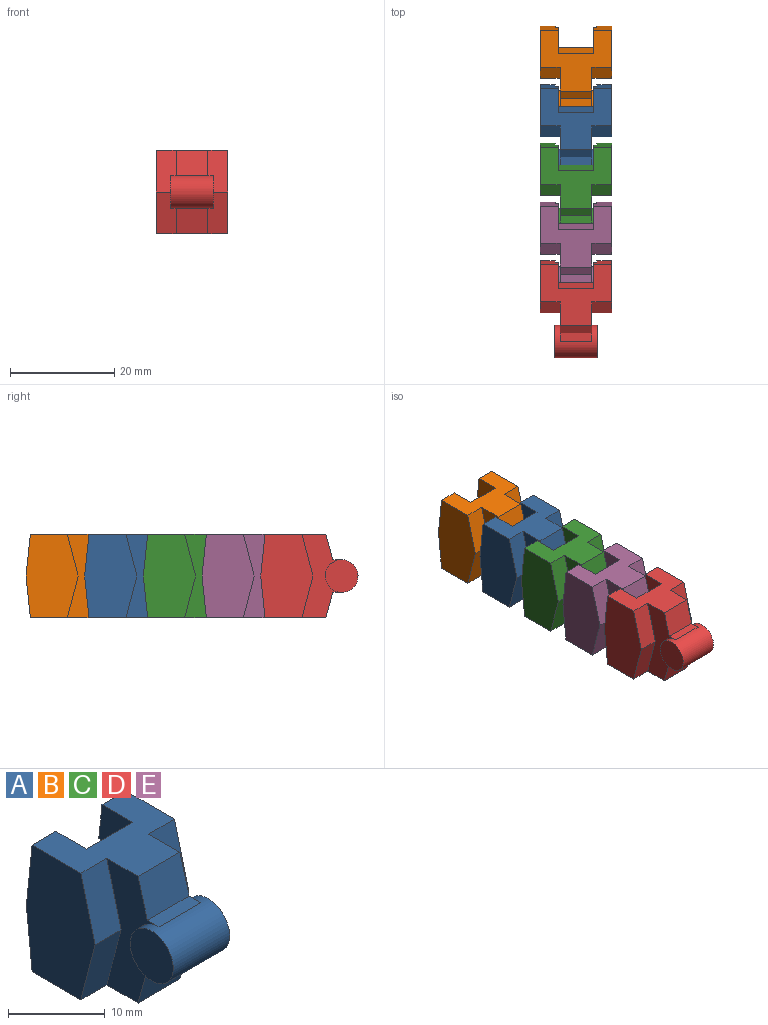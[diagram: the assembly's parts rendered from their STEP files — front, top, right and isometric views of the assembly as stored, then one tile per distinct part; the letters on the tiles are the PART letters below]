
ASSEMBLY  parts=5 mates=4
PART A: 36 faces, bbox 13.7x18.7x16 mm
  f0: plane 8x3.47mm, normal (0,0.99,-0.1), area 25.7mm2, adj f8,f12,f17,f21,f23,f24
  f1: plane 8x3.47mm, normal (0,0.99,-0.1), area 25.7mm2, adj f9,f11,f18,f21,f23,f25
  f2: cylinder r=3.14mm len=8.23mm, axis (-1,0,0), area 102.1mm2, adj f3,f4,f5,f6,f19,f31
  f3: plane 6.27x6.27mm, normal (1,0,0), area 30.9mm2, adj f2
  f4: plane 6.27x6.27mm, normal (-1,0,0), area 30.9mm2, adj f2
  f5: plane 16x7.62mm, normal (1,0,0), area 66.7mm2, adj f2,f10,f19,f20,f21,f27,f31,f32
  f6: plane 16x7.62mm, normal (-1,0,0), area 66.7mm2, adj f2,f7,f19,f20,f21,f26,f31,f32
  f7: plane 8x3.78mm, normal (0,-0.97,-0.25), area 31.3mm2, adj f6,f8,f21,f26
  f8: plane 16x10.03mm, normal (-1,0,0), area 137.2mm2, adj f0,f7,f21,f24,f26,f33
  f9: plane 16x10.03mm, normal (1,0,0), area 137.2mm2, adj f1,f10,f21,f25,f27,f33
  f10: plane 8x3.78mm, normal (0,-0.97,-0.25), area 31.3mm2, adj f5,f9,f21,f27
  f11: plane 7.04x4.29mm, normal (-1,0,0), area 9.5mm2, adj f1,f15,f23,f25,f35
  f12: plane 7.04x4.29mm, normal (1,0,0), area 9.5mm2, adj f0,f15,f23,f24,f35
  f13: plane 7.04x7.04mm, normal (1,0,0), area 38.9mm2, adj f15
  f14: plane 7.04x7.04mm, normal (-1,0,0), area 38.9mm2, adj f15
  f15: cylinder r=3.52mm len=9.3mm, axis (-1,0,0), area 117.3mm2, adj f11,f12,f13,f14,f23,f35
  f16: plane 6.73x0.11mm, normal (0,1,0), area 0.8mm2, adj f17,f18,f22,f23
  f17: plane 4.94x4.48mm, normal (1,0,0), area 18.6mm2, adj f0,f16,f21,f22,f23
  f18: plane 4.94x4.48mm, normal (-1,0,0), area 18.6mm2, adj f1,f16,f21,f22,f23
  f19: plane 6.1x1.7mm, normal (0,0,-1), area 10.4mm2, adj f2,f5,f6,f20
  f20: plane 6.1x4.86mm, normal (0,-0.96,-0.27), area 30.8mm2, adj f5,f6,f19,f21
  f21: plane 13.67x11.68mm, normal (0,0,-1), area 95mm2, adj f0,f1,f5,f6,f7,f8,f9,f10
  f22: plane 6.73x4.37mm, normal (0,0.97,-0.24), area 30.3mm2, adj f16,f17,f18,f21
  f23: plane 7.98x3.92mm, normal (0,0,1), area 5.3mm2, adj f0,f1,f11,f12,f15,f16,f17,f18
  f24: plane 8x3.47mm, normal (0,0.99,0.1), area 25.7mm2, adj f0,f8,f12,f29,f33,f35
  f25: plane 8x3.47mm, normal (0,0.99,0.1), area 25.7mm2, adj f1,f9,f11,f30,f33,f35
  f26: plane 8x3.78mm, normal (0,-0.97,0.25), area 31.3mm2, adj f6,f7,f8,f33
  f27: plane 8x3.78mm, normal (0,-0.97,0.25), area 31.3mm2, adj f5,f9,f10,f33
  f28: plane 6.73x0.11mm, normal (0,1,0), area 0.8mm2, adj f29,f30,f34,f35
  f29: plane 4.94x4.48mm, normal (1,0,0), area 18.6mm2, adj f24,f28,f33,f34,f35
  f30: plane 4.94x4.48mm, normal (-1,0,0), area 18.6mm2, adj f25,f28,f33,f34,f35
  f31: plane 6.1x1.7mm, normal (0,0,1), area 10.4mm2, adj f2,f5,f6,f32
  f32: plane 6.1x4.86mm, normal (0,-0.96,0.27), area 30.8mm2, adj f5,f6,f31,f33
  f33: plane 13.67x11.68mm, normal (0,0,1), area 95mm2, adj f5,f6,f8,f9,f24,f25,f26,f27
  f34: plane 6.73x4.37mm, normal (0,0.97,0.24), area 30.3mm2, adj f28,f29,f30,f33
  f35: plane 7.98x3.92mm, normal (0,0,-1), area 5.3mm2, adj f11,f12,f15,f24,f25,f28,f29,f30
PART B: same geometry as A
PART C: same geometry as A
PART D: same geometry as A
PART E: same geometry as A
PLACE A rot(axis=(1,0,0),0deg) t=(0,39.37,0)mm
PLACE B t=(0,50.65,0)mm
PLACE C rot(axis=(1,0,0),0deg) t=(0,28.09,0)mm
PLACE D t=(0,5.54,0)mm
PLACE E t=(0,16.81,0)mm
MATE cylindrical A.f2 <-> C.f15  axis (-1,0,0) through (0,33.83,0)mm
MATE cylindrical B.f2 <-> A.f15  axis (-1,0,0) through (0,45.11,0)mm
MATE cylindrical E.f2 <-> D.f15  axis (-1,0,0) through (0,11.28,0)mm
MATE cylindrical E.f15 <-> C.f2  axis (-1,0,0) through (0,22.56,0)mm
